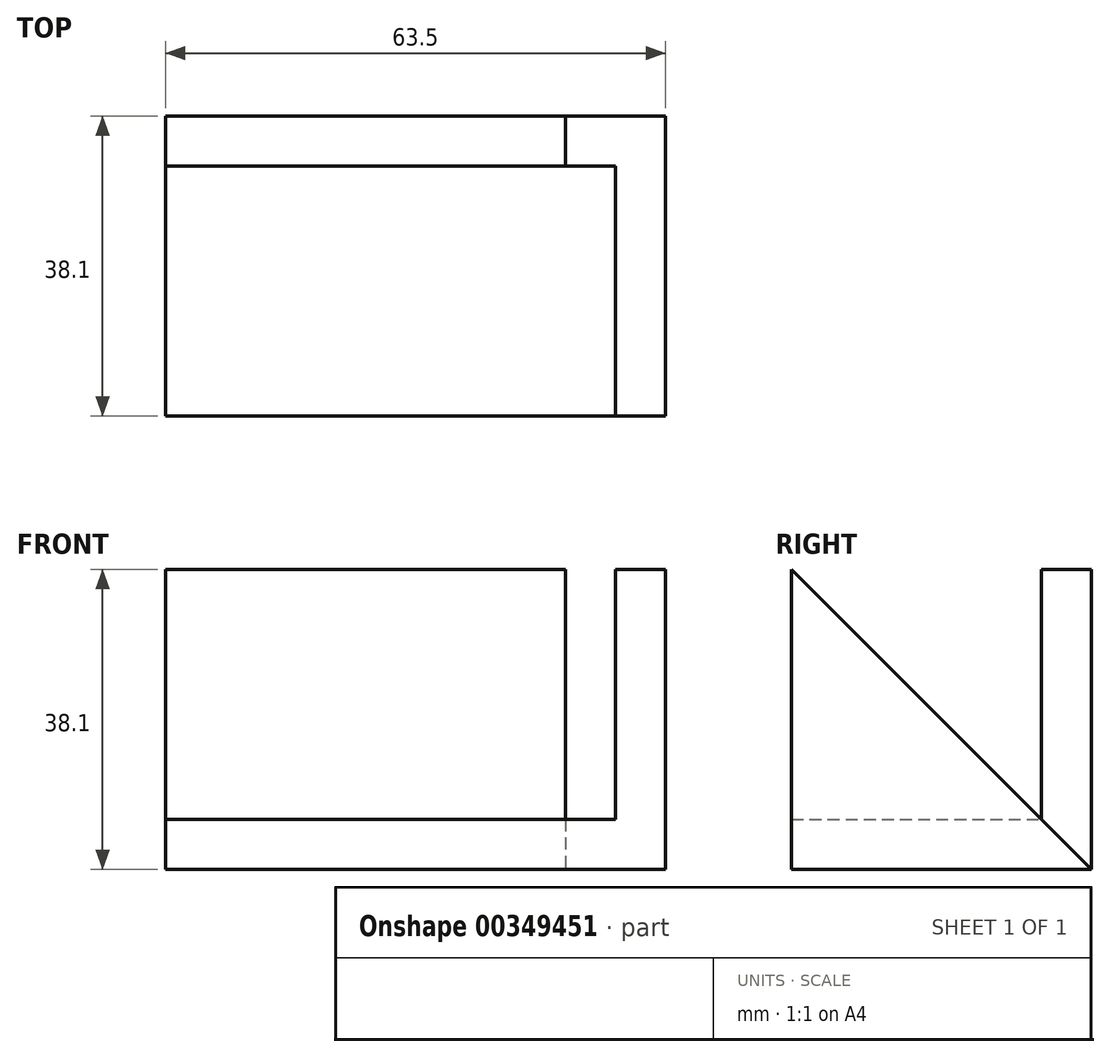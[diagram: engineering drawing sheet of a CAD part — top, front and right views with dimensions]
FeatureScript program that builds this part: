
annotation { "Feature Type Name" : "Feature", "Feature Type Description" : "" }
export const myFeature = defineFeature(function(context is Context, id is Id, definition is map)
    precondition{}
    {
        {
            var Q0;
            Q0=qCreatedBy(makeId("Top.planeOp"),FACE);
            var sketch = newSketch(context, id + "F0", { "sketchPlane" : qUnion([Q0])});
            skLineSegment(sketch, "E0.bottom", {"start": v(31.75, -19.05) * mm, "end": v(-31.75, -19.05) * mm});
            skLineSegment(sketch, "E0.top", {"start": v(31.75, 19.05) * mm, "end": v(-31.75, 19.05) * mm});
            skLineSegment(sketch, "E0.left", {"start": v(31.75, -19.05) * mm, "end": v(31.75, 19.05) * mm});
            skLineSegment(sketch, "E0.right", {"start": v(-31.75, -19.05) * mm, "end": v(-31.75, 19.05) * mm});
            skPoint(sketch, "E0.middle", {"position": v(0, 0) * mm});
            skSolve(sketch);
        }
        {
            var Q0;
            Q0=qSketchRegion(id+"F0",true);
            extrude(context, id + "F1", {"entities" : qUnion([Q0]), "depth" : 6.35 * mm});
        }
        {
            var Q0;
            Q0=makeQuery(id+"F1.opExtrude","CAP_FACE",FACE,{"disambiguationData":[OSD([sQuery(id+"F0.wireOp",EDGE,"E0.bottom"),sQuery(id+"F0.wireOp",EDGE,"E0.top"),sQuery(id+"F0.wireOp",EDGE,"E0.left"),sQuery(id+"F0.wireOp",EDGE,"E0.right")])],"isStart":false});
            var sketch = newSketch(context, id + "F2", { "sketchPlane" : qUnion([Q0])});
            skLineSegment(sketch, "E1.bottom", {"start": v(-31.75, 19.05) * mm, "end": v(19.05, 19.05) * mm});
            skLineSegment(sketch, "E1.top", {"start": v(-31.75, 12.7) * mm, "end": v(31.75, 12.7) * mm});
            skLineSegment(sketch, "E1.left", {"start": v(-31.75, 19.05) * mm, "end": v(-31.75, 12.7) * mm});
            skLineSegment(sketch, "E1.right", {"start": v(19.05, 19.05) * mm, "end": v(19.05, 12.7) * mm});
            skSolve(sketch);
        }
        {
            var Q0;
            Q0=makeQuery(id+"F2.imprint","IMPRINT",FACE,{"disambiguationData":[TD([[makeQuery(id+"F2.imprint","IMPRINT",EDGE,{"derivedFrom":sQuery(id+"F2.wireOp",EDGE,"E1.bottom")}),1.0]])]});
            extrude(context, id + "F3", {"entities" : qUnion([Q0]), "operationType" : NewBodyOperationType.ADD, "depth" : 31.75 * mm});
        }
        {
            var Q0;
            Q0=makeQuery(id+"F1.opExtrude","SWEPT_FACE",FACE,{"disambiguationData":[OSD([sQuery(id+"F0.wireOp",EDGE,"E0.left")])]});
            var sketch = newSketch(context, id + "F4", { "sketchPlane" : qUnion([Q0])});
            skLineSegment(sketch, "E2", {"start": v(19.05, 0) * mm, "end": v(-19.05, 38.1) * mm});
            skLineSegment(sketch, "E3", {"start": v(-19.05, 38.1) * mm, "end": v(-19.05, 0) * mm});
            skLineSegment(sketch, "E4", {"start": v(-19.05, 0) * mm, "end": v(19.05, 0) * mm});
            skSolve(sketch);
        }
        {
            var Q0;
            {var subQ0=sQuery(id+"F4.wireOp",EDGE,"E3");var subQ1=sQuery(id+"F4.wireOp",EDGE,"E2");var subQ2=makeQuery(id+"F4.imprint","INTERSECT",VERTEX,{"derivedFrom":[subQ1,subQ0]});Q0=makeQuery(id+"F4.imprint","IMPRINT",FACE,{"disambiguationData":[TD([[makeQuery(id+"F4.imprint","IMPRINT",EDGE,{"disambiguationData":[TD([[subQ2,1.0]])],"derivedFrom":subQ1}),1.0]])]});}
            var Q1;
            Q1=sQuery(id+"F4.wireOp",EDGE,"E2");
            extrude(context, id + "F5", {"entities" : qUnion([Q0]), "operationType" : NewBodyOperationType.ADD, "surfaceEntities" : qUnion([Q1]), "oppositeDirection" : true, "depth" : 6.35 * mm});
        }
        {
            var Q0;
            {var subQ0=sQuery(id+"F0.wireOp",EDGE,"E0.left");Q0=makeQuery(id+"F5.boolean.opBoolean","MERGE",FACE,{"derivedFrom":[makeQuery(id+"F1.opExtrude","SWEPT_FACE",FACE,{"disambiguationData":[OSD([subQ0])]}),makeQuery(id+"F5.opExtrude","CAP_FACE",FACE,{"disambiguationData":[OSD([subQ0,sQuery(id+"F4.wireOp",EDGE,"E2"),sQuery(id+"F4.wireOp",EDGE,"E3")])],"isStart":true})]});}
            var sketch = newSketch(context, id + "F6", { "sketchPlane" : qUnion([Q0])});
            skLineSegment(sketch, "E5", {"start": v(12.7, 6.35) * mm, "end": v(19.05, 0) * mm});
            skLineSegment(sketch, "E6", {"start": v(19.05, 0) * mm, "end": v(19.05, 6.35) * mm});
            skLineSegment(sketch, "E7", {"start": v(19.05, 6.35) * mm, "end": v(12.7, 6.35) * mm});
            skSolve(sketch);
        }
        {
            var Q0;
            Q0=makeQuery(id+"F6.imprint","IMPRINT",FACE,{"disambiguationData":[TD([[makeQuery(id+"F6.imprint","IMPRINT",EDGE,{"derivedFrom":sQuery(id+"F6.wireOp",EDGE,"E5")}),1.0]])]});
            var Q1;
            Q1=makeQuery(id+"F3.opExtrude","CAP_VERTEX",VERTEX,{"disambiguationData":[OSD([sQuery(id+"F0.wireOp",EDGE,"E0.top"),sQuery(id+"F2.wireOp",EDGE,"E1.bottom"),sQuery(id+"F2.wireOp",EDGE,"E1.right")])],"isStart":true});
            extrude(context, id + "F7", {"entities" : qUnion([Q0]), "operationType" : NewBodyOperationType.REMOVE, "oppositeDirection" : true, "endBoundEntityVertex" : qUnion([Q1]), "depth" : 12.7 * mm});
        }
    });
